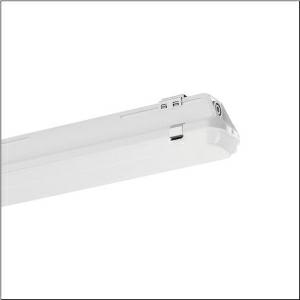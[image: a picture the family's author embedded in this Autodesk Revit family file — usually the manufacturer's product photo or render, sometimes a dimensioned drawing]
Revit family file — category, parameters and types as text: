
# Revit family: monsun_r__21_emergency_51fb107p467c3g_1234
name_source: partatom
category: Lighting Fixtures
units: mm (PartAtom-declared; Revit-internal decimal feet)

## family parameters
Cut with Voids When Loaded = No
Host = Face
Light Source = No
Part Type = Normal
Room Calculation Point = No
Round Connector Dimension = Use Diameter
Shared = No

## types (1)
- --- (1 x LED, 910 lm, 7.1 W, 4000K)
    Apparent Load = 7 VA
    CIE Flux Codes = 47 77 93 94 100
    Color Rendering = 80
    Color Temperature = 4000K
    Default Elevation = 1800 mm
    Description = Monsun® 21 emergency, damp-proof luminaire, chain hanger, primary optical cover: enclosure, of PMMA, light emission: direct distribution, primary light characteristic: symmetric, installation type: suspended mounting, surface-mounted, horizontal mounting, vertical mounting, LED, rated luminous flux: 6.060lm, luminous efficacy: 178lm/W, light colour: 840, colour temperature: 4000K, control gear: ON/OFF, with terminal, 4-pole, max. 2.5mm², mains connection: 220..240V, AC, 50/60Hz, rated input power: 38W, control gear: single battery element, battery: LiFePO4, 9Ah, housing, of glass-fibre reinforced polyester, uncoated, bright grey, incl. chain hanger, length: 1.590mm, width: 90mm, height: 88mm, clip for enclosure, of stainless steel (V2A), ceiling mounting element, of stainless steel (V2A), chain hanger, of stainless steel (V2A), protection rating (complete): IP66, insulation class (complete): insulation class I (protective earthing), certification: CE, UKCA, protection symbol: D, impact resistance: IK04, permissible operating ambient temperature: +5..+25°C, standard: EN 50419, EN 60598-2-1, EN 60598-2-22, corresponds to IFS (International Featured Standards) requirements for safety and quality in the food industry, for indoor or canopied outdoor use, no direct snow, no direct sun, no direct rain, LABS conformity tested according to VDMA 24364:2018-05, contact your sales advisor before using the luminaires in applications with unclear chemical exposure, large temperature fluctuations or condensation-forming humidity, packaging unit: 1 piece
    Height = 89 mm
    Lamp = 1 x LED
    Lamp Light Flux = 910 lm
    Lamp Power = 7.1 W
    Lamp count = 1
    Length = 1590 mm
    Luminous efficacy = 128 lm/W
    Manufacturer = Siteco
    ModVariant = No
    Model = 51FB107P467C3G
    Mounting Place = Ceiling
    Mounting Type = Surface mounted
    Number of Poles = 1
    OnlyDefault = Yes
    Power Factor = 1
    Product Name = Monsun® 21 emergency
    Product group = damp-proof luminaire
    ProductGroupID = 301
    Protection Class = Protection class I
    Protection Degree = IP 66
    RLX_Detail_Level = 1
    RLX_Emergency_Light_Flux = 0 lm
    RLX_Emergency_Type = 0
    RLX_Emergency_Type_DB = No
    RlxData = <blob elided: 88889 chars, md5=f1863edc>
    Socket = socket
    Standby Power = 0 W
    System Light Flux = 910 lm
    System Power = 7 W
    Type Comments = : emergency light operation: 3 h
    Type Image = l_1319656.jpg
    URL = http://relux.com
    VarID = @adj_051771
    Voltage = 0 V
    Weight = 0.00 kg
    Width = 90 mm

## geometry (parser evidence)
native form markers: Blend x4, Sweep x12
no freeform markers — native parametric forms only
